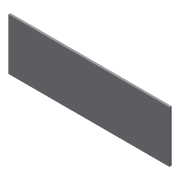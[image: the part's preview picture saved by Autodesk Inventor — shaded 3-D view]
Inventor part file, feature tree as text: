
AUTODESK INVENTOR PART (.ipt)
format: ipt  version: 2016 (Build 200138000, 138)  size: 67,584 bytes
history: native  units: mm
features: extrude x1, sketch x1
ambient origin geometry x8: Origin, YZ Plane, XZ Plane, XY Plane, X Axis, Y Axis, Z Axis, Center Point
bodies: Solid1 (feature_tree)
feature tree (2):
  extrude  "Extrusion1"  Depth=779.45mm TaperAngle=0.0deg
  sketch  "Sketch1"  dims[d4=10.0mm d5=779.45mm d6=0.0mm]
